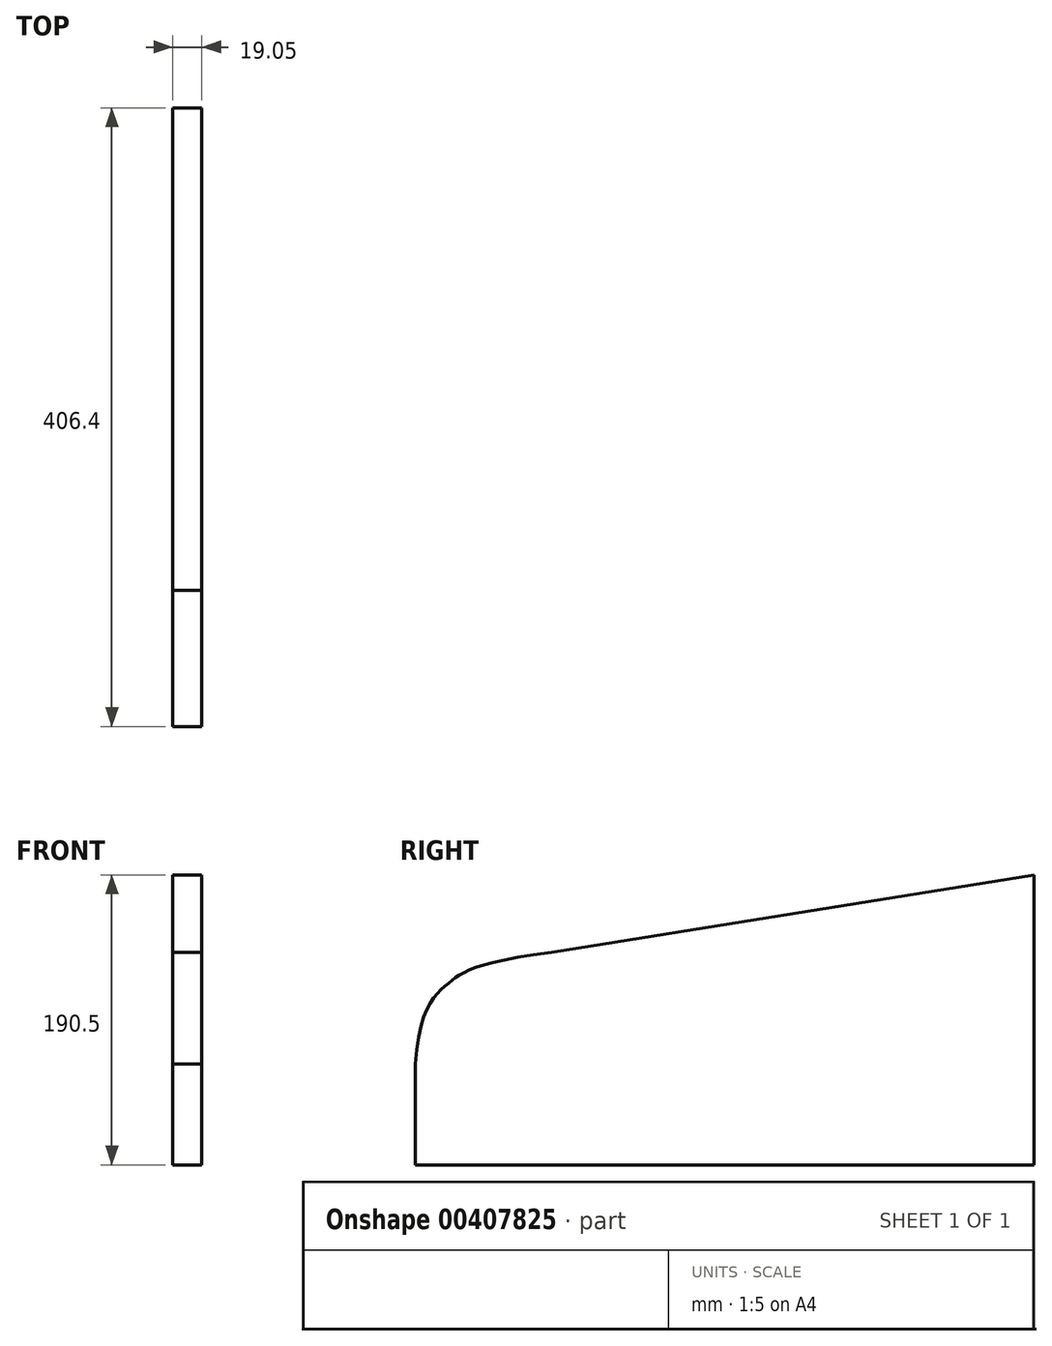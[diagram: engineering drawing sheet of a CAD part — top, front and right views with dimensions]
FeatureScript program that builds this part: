
annotation { "Feature Type Name" : "Feature", "Feature Type Description" : "" }
export const myFeature = defineFeature(function(context is Context, id is Id, definition is map)
    precondition{}
    {
        {
            var Q0;
            Q0=qCreatedBy(makeId("Right.planeOp"),FACE);
            var sketch = newSketch(context, id + "F0", { "sketchPlane" : qUnion([Q0])});
            skLineSegment(sketch, "E0", {"start": v(195.89, -80.73) * mm, "end": v(-210.51, -80.73) * mm});
            skLineSegment(sketch, "E1", {"start": v(195.89, -80.73) * mm, "end": v(195.89, 109.77) * mm});
            skLineSegment(sketch, "E2", {"start": v(195.89, 109.77) * mm, "end": v(-121.16, 58.97) * mm});
            skLineSegment(sketch, "E3", {"start": v(-210.51, -80.73) * mm, "end": v(-210.51, -14.45) * mm});
            skFitSpline(sketch, "E4", {"points": [v(-121.16, 58.97) * mm, v(-189.14, 38.25) * mm, v(-210.51, -14.45) * mm], "startDerivative": vector(-294.58, -40.2) * mm, "endDerivative": vector(-15.36, -237.75) * mm});
            skSolve(sketch);
        }
        {
            var Q0;
            Q0=makeQuery(id+"F0.imprint","IMPRINT",FACE,{"disambiguationData":[TD([[makeQuery(id+"F0.imprint","IMPRINT",EDGE,{"derivedFrom":sQuery(id+"F0.wireOp",EDGE,"E0")}),-1.0]])]});
            extrude(context, id + "F1", {"entities" : qUnion([Q0]), "depth" : 19.05 * mm});
        }
    });
